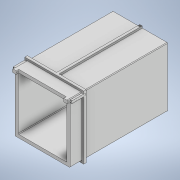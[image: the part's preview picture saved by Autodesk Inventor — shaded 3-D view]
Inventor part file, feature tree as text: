
AUTODESK INVENTOR PART (.ipt)
format: ipt  version: 2021 (Build 250183000, 183)  size: 258,048 bytes
history: native  units: mm
features: extrude x12, sketch x11, other x1
ambient origin geometry x8: Origin, YZ Plane, XZ Plane, XY Plane, X Axis, Y Axis, Z Axis, Center Point
bodies: Body1 (feature_tree)
feature tree (24):
  other  "Sólido1"
  sketch  "Boceto1"  dims[d11=50.0mm d12=0.0mm d17=5.0mm]
  extrude  "Extrusión1"  Depth=5.0mm
  extrude  "Extrusión2"  Depth=20.0mm TaperAngle=0.0deg
  extrude  "Extrusión3"  Depth=470.0mm
  extrude  "Extrusión4"  Depth=15.0mm TaperAngle=0.0deg
  extrude  "Extrusión5"  Depth=20.0mm
  extrude  "Extrusión6"  Depth=20.0mm
  extrude  "Extrusión7"  Depth=20.0mm
  extrude  "Extrusión9"  Depth=20.0mm
  extrude  "Extrusión10"  Depth=110.0mm TaperAngle=0.0deg
  extrude  "Extrusión11"  Depth=20.0mm
  extrude  "Extrusión12"  [1 undecoded]
  extrude  "Extrusión13"  [1 undecoded]
  sketch  "Boceto2"  dims[d18=770.0mm d19=0.0mm d21=20.0mm d22=0.0mm]
  sketch  "Boceto3"  dims[d24=0.0mm d25=0.0mm d26=470.0mm]
  sketch  "Boceto4"  dims[d27=385.0mm d37=15.0mm d38=0.0mm]
  sketch  "Boceto5"  dims[d39=435.0mm d40=20.0mm]
  sketch  "Boceto6"  dims[d41=15.0mm d42=0.0mm d43=20.0mm]
  sketch  "Boceto8"  dims[d44=15.0mm d45=0.0mm d48=20.0mm]
  sketch  "Boceto9"  dims[d49=15.0mm d50=0.0mm d51=20.0mm]
  sketch  "Boceto10"  dims[d52=15.0mm d53=0.0mm d54=110.0mm d55=0.0mm]
  sketch  "Boceto11"  dims[d56=110.0mm d57=0.0mm d58=20.0mm]
  sketch  "Boceto12"  dims[d59=13.25mm d60=0.0mm]
note: 2 required parameter values undecoded (feature->parameter linkage not recoverable at this tier; creation-order binding heuristic only, values carry confidence <= 0.55)
